# Revit family: pf-rp224_280ea_60Hz
name_source: partatom
category: 機械設備
units: mm (PartAtom-declared; Revit-internal decimal feet)

## family parameters
OmniClass タイトル = Split System Air Conditioning Units
OmniClass 番号 = 23.75.10.24.21.27.27
パーツ タイプ = 標準
ロード時にボイドで切り取り = いいえ
丸型コネクタ寸法 = 直径を使用
作業面ベース = いいえ
共有 = いいえ
常に垂直 = はい
部屋計算ポイント = いいえ

## types (2) — shared parameters
Clearance Back = 50  [stored 0.164042 ft]
Clearance Front = 900
Clearance Left = 100  [stored 0.328084 ft]
Clearance Right = 100  [stored 0.328084 ft]
Clearance Top = 300
Depth = 400  [stored 1.31234 ft]
Height = 1850  [stored 6.06955 ft]
IfcExportAs = IfcUnitaryEquipmentType
IfcExportType = AIRCONDITIONINGUNIT
OmniClassCode = 23-33 17 13 11
S寸法 = 50  [stored 0.164042 ft]
URL = https://www.mitsubishielectric.co.jp
Uniclass2015Code = Pr_70_65_03_84
Uniclass2015Title = Split coil remote air cooled condensing units
Uniclass2015Version = Systems v1.9
サービススペース = はい
ドレン管径 = 26.00 mm
仕様書バージョン = Version1.0
冷媒ガス管径 = 25.40 mm
冷媒管径 = 100.00 mm
冷媒高低圧ガス管径 = 0.00 mm
分類コード = 50053003123100
加湿給水管径 = 0.00 mm
参照している仕様書等のバージョン = 公共建築工事標準仕様書（機械設備工事編）平成31年度版
周波数 = 60 Hz
呼称 = 室内機_床置(露出)⽴形(直吹)
始動方式 = 直入
形式 = 床置（露出）立形
推奨ブレーカー容量 = 0 A
最大電流値 = 0 A
本体マテリアル = <カテゴリ別>
極数 = 3
機外静圧 = 0.0 Pa
法定耐用年数 = 15
消費電力_加湿器 = 0 W
消費電力_電気ヒーター = 0 W
相 = 1
相_電気ヒーター = 1
積算_科目 = 1 空気調和設備
符号 = PAC-FRV(J)
製品リリース年月 = 2021年6月23日
製品出荷対象 = 国内
製造元 = 三菱電機株式会社
設置方法 = 床置形
説明 = 店舗・事務所用パッケージエアコン(Mr.SLIM) 床置形
負荷分類 = 3_ファン類
運転質量 = 0.00 kg
電動機出力_圧縮機 = 0 W
電動機出力_送風機 = 375 W
電圧 = 200 V
電圧_電気ヒーター = 0 V
zero-valued in all types: APF, COP, 価格, 有効加湿量, 機械基礎_D, 機械基礎_H, 機械基礎_W

## per-type parameters (varying)
- PF-RP280EA: MAX風量=4380.0 m³/h; MID風量=4020.0 m³/h; MIN風量=3660.0 m³/h; MIN風量2=3300.0 m³/h; Width=1200; 冷媒液管径=12.70 mm; 冷媒管径符号=Cg; 冷房能力=25 kW; 暖房能力=28 kW; 消費電力=500 W; 消費電力_冷房=500 W; 消費電力_暖房=500 W; 製品質量=111.00 kg; 質量=133.20 kg; 音響パワーレベル(dB)=72; 風量=4380.0 m³/h; 風量（m3／min）=73; 風量（中）（m3／min）=67; 風量（弱）（m3／min）=61; 風量（静）（m3／min）=55; 騒音レベル（中）(dB)=70; 騒音レベル（弱）(dB)=69; 騒音レベル（強）(dB)=72; 騒音レベル（静）(dB)=68
- PF-RP224EA: MAX風量=3180.0 m³/h; MID風量=2940.0 m³/h; MIN風量=2760.0 m³/h; MIN風量2=2520.0 m³/h; Width=985  [stored 3.23163 ft]; 企業コード=108420; 冷媒液管径=9.52 mm; 冷媒管径符号=Bg; 冷房能力=20 kW; 暖房能力=22 kW; 消費電力=300 W; 消費電力_冷房=300 W; 消費電力_暖房=300 W; 製品質量=100.00 kg; 質量=120.00 kg; 音響パワーレベル(dB)=68; 風量=3180.0 m³/h; 風量（m3／min）=53; 風量（中）（m3／min）=49; 風量（弱）（m3／min）=46; 風量（静）（m3／min）=42; 騒音レベル（中）(dB)=67; 騒音レベル（弱）(dB)=66; 騒音レベル（強）(dB)=68; 騒音レベル（静）(dB)=65

note: column(s) folded — value = type name in every type: モデル

note: [stored X ft] marks values corroborated as IEEE doubles in the binary element streams (Revit-internal decimal feet)

## geometry (parser evidence)
native form markers: Blend x2
no freeform markers — native parametric forms only
